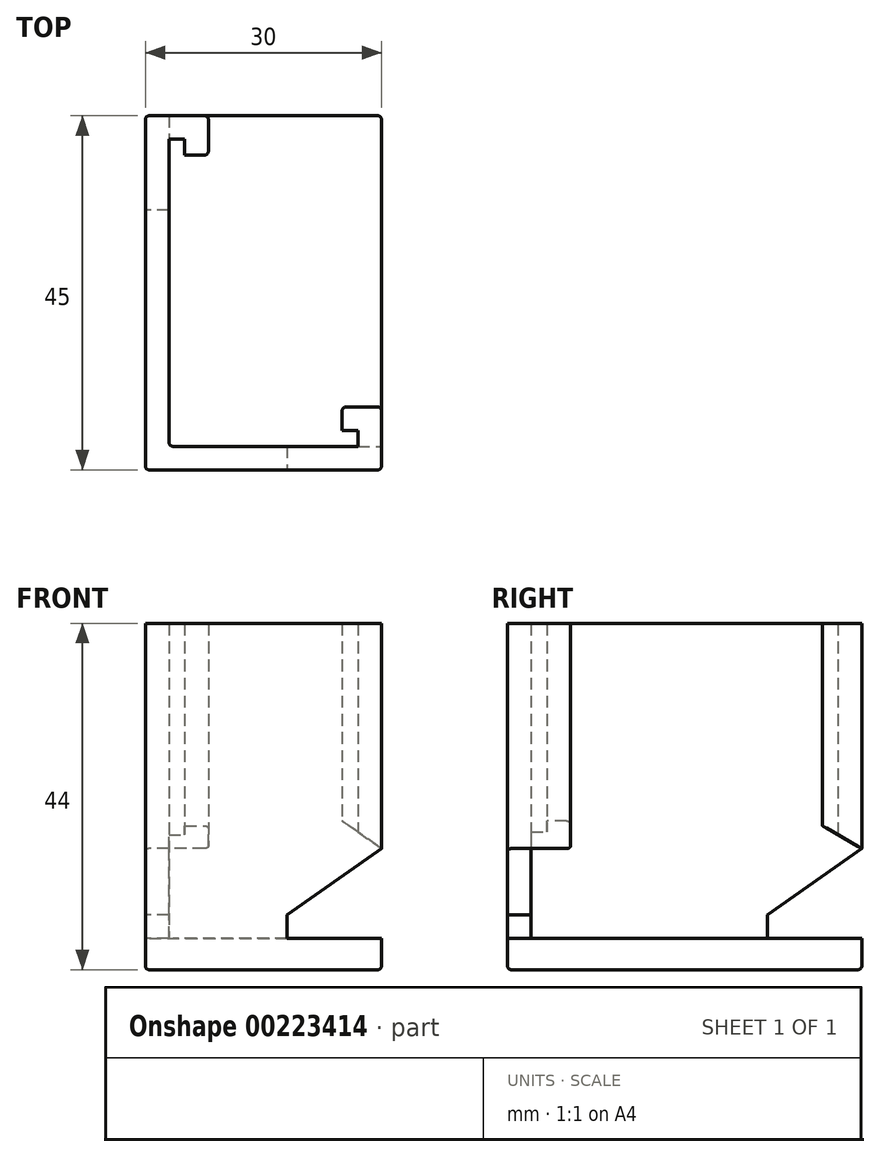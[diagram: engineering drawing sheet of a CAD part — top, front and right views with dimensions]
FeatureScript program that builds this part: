
annotation { "Feature Type Name" : "Feature", "Feature Type Description" : "" }
export const myFeature = defineFeature(function(context is Context, id is Id, definition is map)
    precondition{}
    {
        {
            var Q0;
            Q0=qCreatedBy(makeId("Top.planeOp"),FACE);
            var sketch = newSketch(context, id + "F0", { "sketchPlane" : qUnion([Q0])});
            skLineSegment(sketch, "E0", {"start": v(30, 0) * mm, "end": v(0, 0) * mm});
            skLineSegment(sketch, "E1", {"start": v(0, 0) * mm, "end": v(0, 45) * mm});
            skLineSegment(sketch, "E2", {"start": v(0, 45) * mm, "end": v(8, 45) * mm});
            skLineSegment(sketch, "E3", {"start": v(8, 45) * mm, "end": v(8, 40) * mm});
            skLineSegment(sketch, "E4", {"start": v(25, 8) * mm, "end": v(30, 8) * mm});
            skLineSegment(sketch, "E5", {"start": v(30, 8) * mm, "end": v(30, 0) * mm});
            skLineSegment(sketch, "E6.0", {"start": v(5, 42) * mm, "end": v(5, 40) * mm});
            skLineSegment(sketch, "E6.1", {"start": v(3, 42) * mm, "end": v(5, 42) * mm});
            skLineSegment(sketch, "E6.2", {"start": v(25, 5) * mm, "end": v(27, 5) * mm});
            skLineSegment(sketch, "E6.3", {"start": v(27, 5) * mm, "end": v(27, 3) * mm});
            skLineSegment(sketch, "E6.4", {"start": v(27, 3) * mm, "end": v(3, 3) * mm});
            skLineSegment(sketch, "E6.5", {"start": v(3, 3) * mm, "end": v(3, 42) * mm});
            skLineSegment(sketch, "E7", {"start": v(5, 40) * mm, "end": v(8, 40) * mm});
            skLineSegment(sketch, "E8", {"start": v(25, 5) * mm, "end": v(25, 8) * mm});
            skSolve(sketch);
        }
        {
            var Q0;
            Q0 = qSketchRegion(id + "F0", true);
            extrude(context, id + "F1", {"entities" : qUnion([Q0]), "depth" : 40 * mm});
        }
        {
            var Q0;
            Q0=qCreatedBy(makeId("Top.planeOp"),FACE);
            var sketch = newSketch(context, id + "F2", { "sketchPlane" : qUnion([Q0])});
            skLineSegment(sketch, "E9.0", {"start": v(0, 0) * mm, "end": v(0, 45) * mm});
            skLineSegment(sketch, "E9.1", {"start": v(30, 0) * mm, "end": v(0, 0) * mm});
            skLineSegment(sketch, "E10", {"start": v(0, 45) * mm, "end": v(30, 45) * mm});
            skLineSegment(sketch, "E11", {"start": v(30, 45) * mm, "end": v(30, 0) * mm});
            skSolve(sketch);
        }
        {
            var Q0;
            Q0 = qSketchRegion(id + "F2", true);
            extrude(context, id + "F3", {"entities" : qUnion([Q0]), "operationType" : NewBodyOperationType.ADD, "oppositeDirection" : true, "depth" : 4 * mm});
        }
        {
            var Q0;
            Q0=qCreatedBy(makeId("Front.planeOp"),FACE);
            var sketch = newSketch(context, id + "F4", { "sketchPlane" : qUnion([Q0])});
            skLineSegment(sketch, "E12", {"start": v(30, 0) * mm, "end": v(18, 0) * mm});
            skLineSegment(sketch, "E13", {"start": v(18, 0) * mm, "end": v(18, 3) * mm});
            skLineSegment(sketch, "E14", {"start": v(18, 3) * mm, "end": v(30, 11.4) * mm});
            skLineSegment(sketch, "E15", {"start": v(30, 11.4) * mm, "end": v(30, 0) * mm});
            skSolve(sketch);
        }
        {
            var Q0;
            Q0 = qSketchRegion(id + "F4", true);
            extrude(context, id + "F5", {"entities" : qUnion([Q0]), "operationType" : NewBodyOperationType.REMOVE, "endBound" : BoundingType.THROUGH_ALL, "oppositeDirection" : true, "depth" : 25 * mm});
        }
        {
            var Q0;
            Q0=makeQuery(id+"F1.opExtrude","SWEPT_FACE",FACE,{"disambiguationData":[OSD([sQuery(id+"F0.wireOp",EDGE,"E6.4")])]});
            var sketch = newSketch(context, id + "F6", { "sketchPlane" : qUnion([Q0])});
            skLineSegment(sketch, "E16.bottom", {"start": v(-18, 19.8) * mm, "end": v(-30, 11.4) * mm});
            skLineSegment(sketch, "E16.top", {"start": v(-18, 3) * mm, "end": v(-30, 3) * mm});
            skLineSegment(sketch, "E16.left", {"start": v(-30, 11.4) * mm, "end": v(-30, 3) * mm});
            skLineSegment(sketch, "E16.right", {"start": v(-18, 19.8) * mm, "end": v(-18, 3) * mm});
            skSolve(sketch);
        }
        {
            var Q0;
            Q0 = qSketchRegion(id + "F6", true);
            extrude(context, id + "F7", {"entities" : qUnion([Q0]), "operationType" : NewBodyOperationType.REMOVE, "endBound" : BoundingType.THROUGH_ALL, "depth" : 25 * mm});
        }
        {
            var Q0;
            Q0=qCreatedBy(makeId("Right.planeOp"),FACE);
            var sketch = newSketch(context, id + "F8", { "sketchPlane" : qUnion([Q0])});
            skLineSegment(sketch, "E17", {"start": v(45, 0) * mm, "end": v(33, 0) * mm});
            skLineSegment(sketch, "E18", {"start": v(33, 0) * mm, "end": v(33, 3) * mm});
            skLineSegment(sketch, "E19", {"start": v(33, 3) * mm, "end": v(45, 11.4) * mm});
            skLineSegment(sketch, "E20", {"start": v(45, 11.4) * mm, "end": v(45, 0) * mm});
            skSolve(sketch);
        }
        {
            var Q0;
            Q0 = qSketchRegion(id + "F8", true);
            extrude(context, id + "F9", {"entities" : qUnion([Q0]), "operationType" : NewBodyOperationType.REMOVE, "endBound" : BoundingType.THROUGH_ALL, "depth" : 25 * mm});
        }
        {
            var Q0;
            Q0=makeQuery(id+"F1.opExtrude","SWEPT_FACE",FACE,{"disambiguationData":[OSD([sQuery(id+"F0.wireOp",EDGE,"E3")])]});
            var sketch = newSketch(context, id + "F10", { "sketchPlane" : qUnion([Q0])});
            skLineSegment(sketch, "E21.0", {"start": v(45, 11.4) * mm, "end": v(40, 7.9) * mm});
            skLineSegment(sketch, "E22", {"start": v(45, 11.4) * mm, "end": v(40, 14.29) * mm});
            skLineSegment(sketch, "E23", {"start": v(40, 7.9) * mm, "end": v(40, 14.29) * mm});
            skSolve(sketch);
        }
        {
            var Q0;
            Q0 = qSketchRegion(id + "F10", true);
            var Q1;
            Q1=makeQuery(id+"F1.opExtrude","SWEPT_FACE",FACE,{"disambiguationData":[OSD([sQuery(id+"F0.wireOp",EDGE,"E6.5")])]});
            extrude(context, id + "F11", {"entities" : qUnion([Q0]), "operationType" : NewBodyOperationType.REMOVE, "endBound" : BoundingType.UP_TO_SURFACE, "oppositeDirection" : true, "endBoundEntityFace" : qUnion([Q1]), "depth" : 25 * mm});
        }
        {
            var Q0;
            Q0=makeQuery(id+"F3.boolean.opBoolean","MERGE",EDGE,{"derivedFrom":[makeQuery(id+"F1.opExtrude","SWEPT_EDGE",EDGE,{"disambiguationData":[OSD([sQuery(id+"F0.wireOp",EDGE,"E1"),sQuery(id+"F0.wireOp",EDGE,"E2")])]}),makeQuery(id+"F3.opExtrude","SWEPT_EDGE",EDGE,{"disambiguationData":[OSD([sQuery(id+"F2.wireOp",EDGE,"E9.0"),sQuery(id+"F2.wireOp",EDGE,"E10")])]})]});
            var Q1;
            Q1=makeQuery(id+"F3.boolean.opBoolean","MERGE",EDGE,{"derivedFrom":[makeQuery(id+"F1.opExtrude","SWEPT_EDGE",EDGE,{"disambiguationData":[OSD([sQuery(id+"F0.wireOp",EDGE,"E0"),sQuery(id+"F0.wireOp",EDGE,"E1")])]}),makeQuery(id+"F3.opExtrude","SWEPT_EDGE",EDGE,{"disambiguationData":[OSD([sQuery(id+"F2.wireOp",EDGE,"E9.0"),sQuery(id+"F2.wireOp",EDGE,"E9.1")])]})]});
            var Q2;
            Q2=makeQuery(id+"F3.boolean.opBoolean","MERGE",EDGE,{"derivedFrom":[makeQuery(id+"F1.opExtrude","SWEPT_EDGE",EDGE,{"disambiguationData":[OSD([sQuery(id+"F0.wireOp",EDGE,"E0"),sQuery(id+"F0.wireOp",EDGE,"E5")])]}),makeQuery(id+"F3.opExtrude","SWEPT_EDGE",EDGE,{"disambiguationData":[OSD([sQuery(id+"F2.wireOp",EDGE,"E9.1"),sQuery(id+"F2.wireOp",EDGE,"E11")])]})]});
            var Q3;
            Q3=makeQuery(id+"F1.opExtrude","SWEPT_EDGE",EDGE,{"disambiguationData":[OSD([sQuery(id+"F0.wireOp",EDGE,"E4"),sQuery(id+"F0.wireOp",EDGE,"E5")])]});
            var Q4;
            Q4=makeQuery(id+"F1.opExtrude","SWEPT_EDGE",EDGE,{"disambiguationData":[OSD([sQuery(id+"F0.wireOp",EDGE,"E3"),sQuery(id+"F0.wireOp",EDGE,"E7")])]});
            var Q5;
            Q5=makeQuery(id+"F1.opExtrude","SWEPT_EDGE",EDGE,{"disambiguationData":[OSD([sQuery(id+"F0.wireOp",EDGE,"E2"),sQuery(id+"F0.wireOp",EDGE,"E3")])]});
            var Q6;
            Q6=makeQuery(id+"F3.opExtrude","CAP_EDGE",EDGE,{"disambiguationData":[OSD([sQuery(id+"F2.wireOp",EDGE,"E11")])],"isStart":true});
            var Q7;
            Q7=makeQuery(id+"F3.opExtrude","CAP_EDGE",EDGE,{"disambiguationData":[OSD([sQuery(id+"F2.wireOp",EDGE,"E11")])],"isStart":false});
            var Q8;
            Q8=makeQuery(id+"F3.opExtrude","CAP_EDGE",EDGE,{"disambiguationData":[OSD([sQuery(id+"F2.wireOp",EDGE,"E10")])],"isStart":true});
            var Q9;
            Q9=makeQuery(id+"F3.opExtrude","CAP_EDGE",EDGE,{"disambiguationData":[OSD([sQuery(id+"F2.wireOp",EDGE,"E10")])],"isStart":false});
            var Q10;
            Q10=makeQuery(id+"F3.opExtrude","SWEPT_EDGE",EDGE,{"disambiguationData":[OSD([sQuery(id+"F2.wireOp",EDGE,"E10"),sQuery(id+"F2.wireOp",EDGE,"E11")])]});
            var Q11;
            Q11=makeQuery(id+"F1.opExtrude","SWEPT_EDGE",EDGE,{"disambiguationData":[OSD([sQuery(id+"F0.wireOp",EDGE,"E4"),sQuery(id+"F0.wireOp",EDGE,"E8")])]});
            var Q12;
            Q12=makeQuery(id+"F3.opExtrude","CAP_EDGE",EDGE,{"disambiguationData":[OSD([sQuery(id+"F2.wireOp",EDGE,"E9.1")])],"isStart":false});
            var Q13;
            Q13=makeQuery(id+"F3.opExtrude","CAP_EDGE",EDGE,{"disambiguationData":[OSD([sQuery(id+"F2.wireOp",EDGE,"E9.0")])],"isStart":false});
            var Q14;
            Q14=makeQuery(id+"F1.opExtrude","SWEPT_EDGE",EDGE,{"disambiguationData":[OSD([sQuery(id+"F0.wireOp",EDGE,"E6.4"),sQuery(id+"F0.wireOp",EDGE,"E6.5")])]});
            fillet(context, id + "F12", {"entities" : qUnion([Q0, Q1, Q2, Q3, Q4, Q5, Q6, Q7, Q8, Q9, Q10, Q11, Q12, Q13, Q14]), "radius" : 0.5 * mm, "tangentPropagation" : true, "allowEdgeOverflow" : false});
        }
    });
